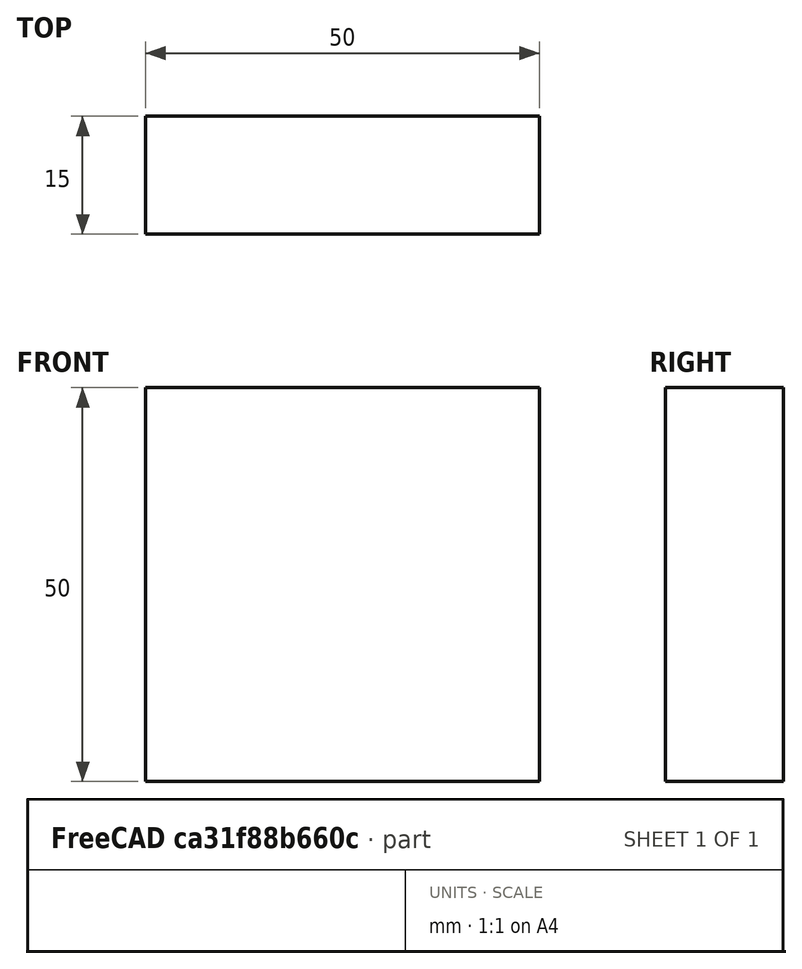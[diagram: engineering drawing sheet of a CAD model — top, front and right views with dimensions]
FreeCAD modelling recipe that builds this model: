
FCSTD DOCUMENT  (FreeCAD 0.15R4671 (Git))
Label: Flat Bar 50x15 EN10058 S235JR
License: All rights reserved
LicenseURL: http://en.wikipedia.org/wiki/All_rights_reserved
objects: Sketcher::SketchObject×1, Part::Extrusion×1
note: 2 computed .brp shape members not serialized (recipe doc carries the construction recipe); baked Part::Feature solids carry a one-line shape summary decoded from their .brp

FEATURE [Sketcher::SketchObject] Sketch
  sketch-geometry (4):
    g0: LineSegment StartX=-25 StartY=-7.5 StartZ=0 EndX=25 EndY=-7.5 EndZ=0
    g1: LineSegment StartX=25 StartY=-7.5 StartZ=0 EndX=25 EndY=7.5 EndZ=0
    g2: LineSegment StartX=25 StartY=7.5 StartZ=0 EndX=-25 EndY=7.5 EndZ=0
    g3: LineSegment StartX=-25 StartY=7.5 StartZ=0 EndX=-25 EndY=-7.5 EndZ=0
  constraints (12):
    c: Coincident(g0,g1)
    c: Coincident(g1,g2)
    c: Coincident(g2,g3)
    c: Coincident(g3,g0)
    c: Horizontal(g0)
    c: Horizontal(g2)
    c: Vertical(g1)
    c: Vertical(g3)
    c: Symmetric(g1,g2,g-2)
    c: Symmetric(g0,g1,g-1)
    c: DistanceY(g1) = 15
    c: DistanceX(g0) = 50
FEATURE [Part::Extrusion] Extrude  label="Flat Bar 50x15 EN10058 S235JR"
  Base = -> Sketch
  Dir = (0,0,50)
  Solid = true
